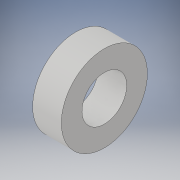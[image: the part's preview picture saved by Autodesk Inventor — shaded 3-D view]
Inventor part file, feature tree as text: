
AUTODESK INVENTOR PART (.ipt)
format: ipt  version: 2019 (Build 230136000, 136)  size: 98,304 bytes
history: native  units: in
note: dims shown in document units (in); Inventor stores cm internally (conversion verified against a paired STEP export)
features: extrude x1, sketch x1
ambient origin geometry x8: Origin, YZ Plane, XZ Plane, XY Plane, X Axis, Y Axis, Z Axis, Center Point
bodies: Solid1 (feature_tree)
feature tree (2):
  extrude  "Extrusion1"  Depth=0.125in
  sketch  "Sketch1"  dims[d0=0.375in d1=0.195in d2=0.125in d3=0.0in]
